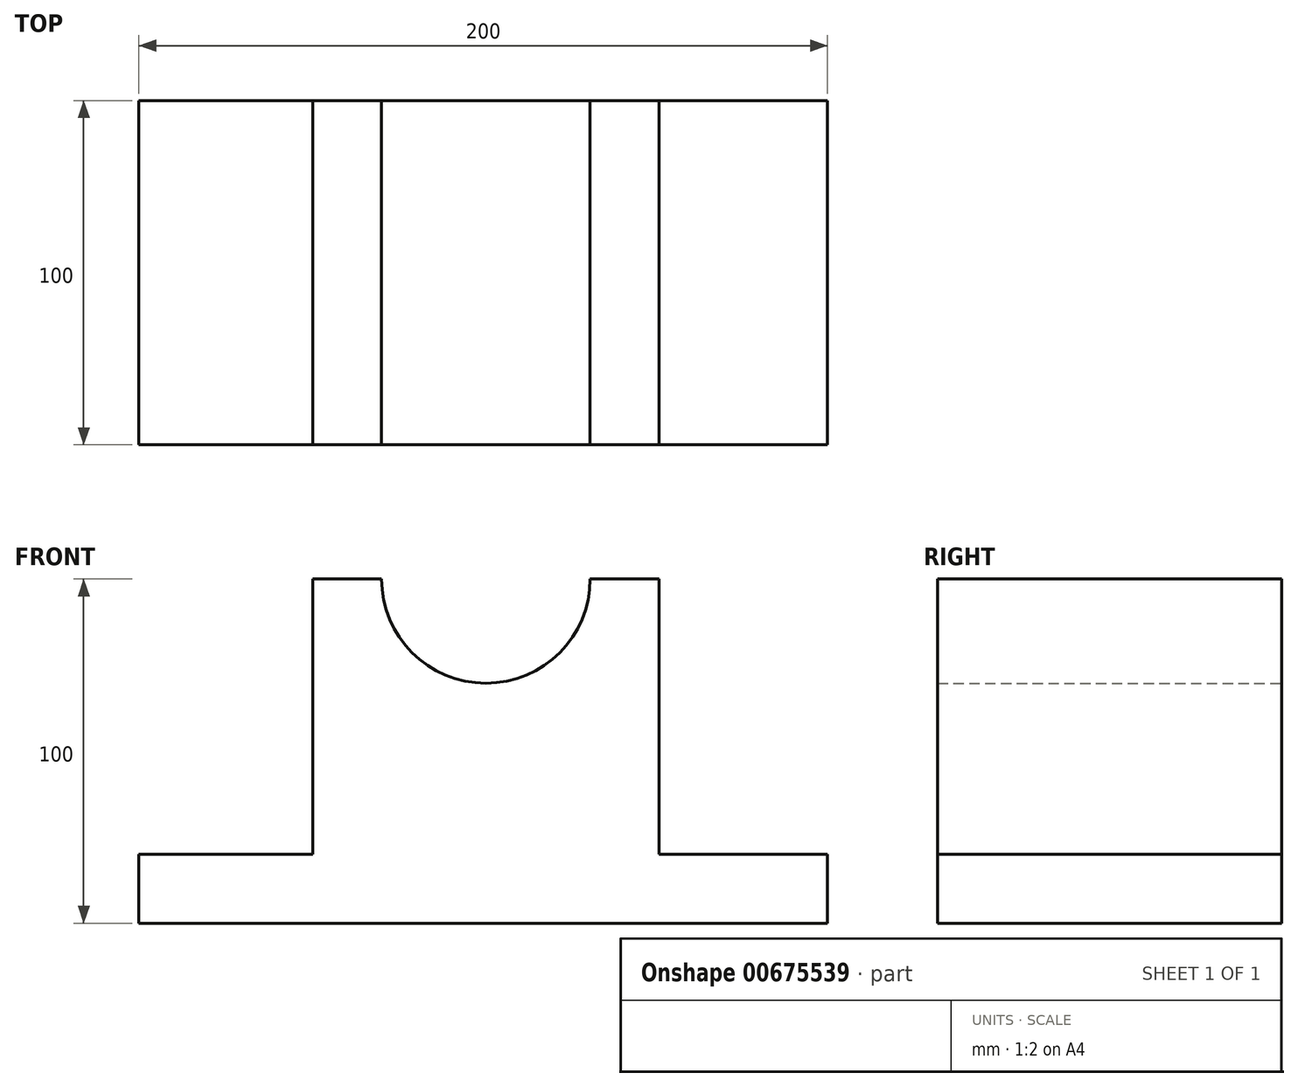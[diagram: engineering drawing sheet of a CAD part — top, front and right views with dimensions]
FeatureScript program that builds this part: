
annotation { "Feature Type Name" : "Feature", "Feature Type Description" : "" }
export const myFeature = defineFeature(function(context is Context, id is Id, definition is map)
    precondition{}
    {
        {
            var Q0;
            Q0=qCreatedBy(makeId("Front.planeOp"),FACE);
            var sketch = newSketch(context, id + "F0", { "sketchPlane" : qUnion([Q0])});
            skLineSegment(sketch, "E0", {"start": v(0, 0) * mm, "end": v(-200, 0) * mm});
            skLineSegment(sketch, "E1", {"start": v(-200, 0) * mm, "end": v(-200, 20) * mm});
            skLineSegment(sketch, "E2", {"start": v(-200, 20) * mm, "end": v(-149.49, 20) * mm});
            skLineSegment(sketch, "E3", {"start": v(-149.49, 20) * mm, "end": v(-149.49, 100) * mm});
            skLineSegment(sketch, "E4", {"start": v(-149.49, 100) * mm, "end": v(-129.49, 100) * mm});
            skLineSegment(sketch, "E5", {"start": v(0, 0) * mm, "end": v(0, 20) * mm});
            skLineSegment(sketch, "E6", {"start": v(0, 20) * mm, "end": v(-48.92, 20) * mm});
            skLineSegment(sketch, "E7", {"start": v(-48.92, 20) * mm, "end": v(-48.92, 100) * mm});
            skLineSegment(sketch, "E8", {"start": v(-48.92, 100) * mm, "end": v(-68.92, 100) * mm});
            skArc(sketch, "E9", {"start": v(-129.49, 100) * mm, "mid": v(-99.2, 69.72) * mm, "end": v(-68.92, 100) * mm});
            skSolve(sketch);
        }
        {
            var Q0;
            Q0 = qSketchRegion(id + "F0", true);
            extrude(context, id + "F1", {"entities" : qUnion([Q0]), "depth" : 100 * mm, "offsetDistance" : 25 * mm});
        }
    });
